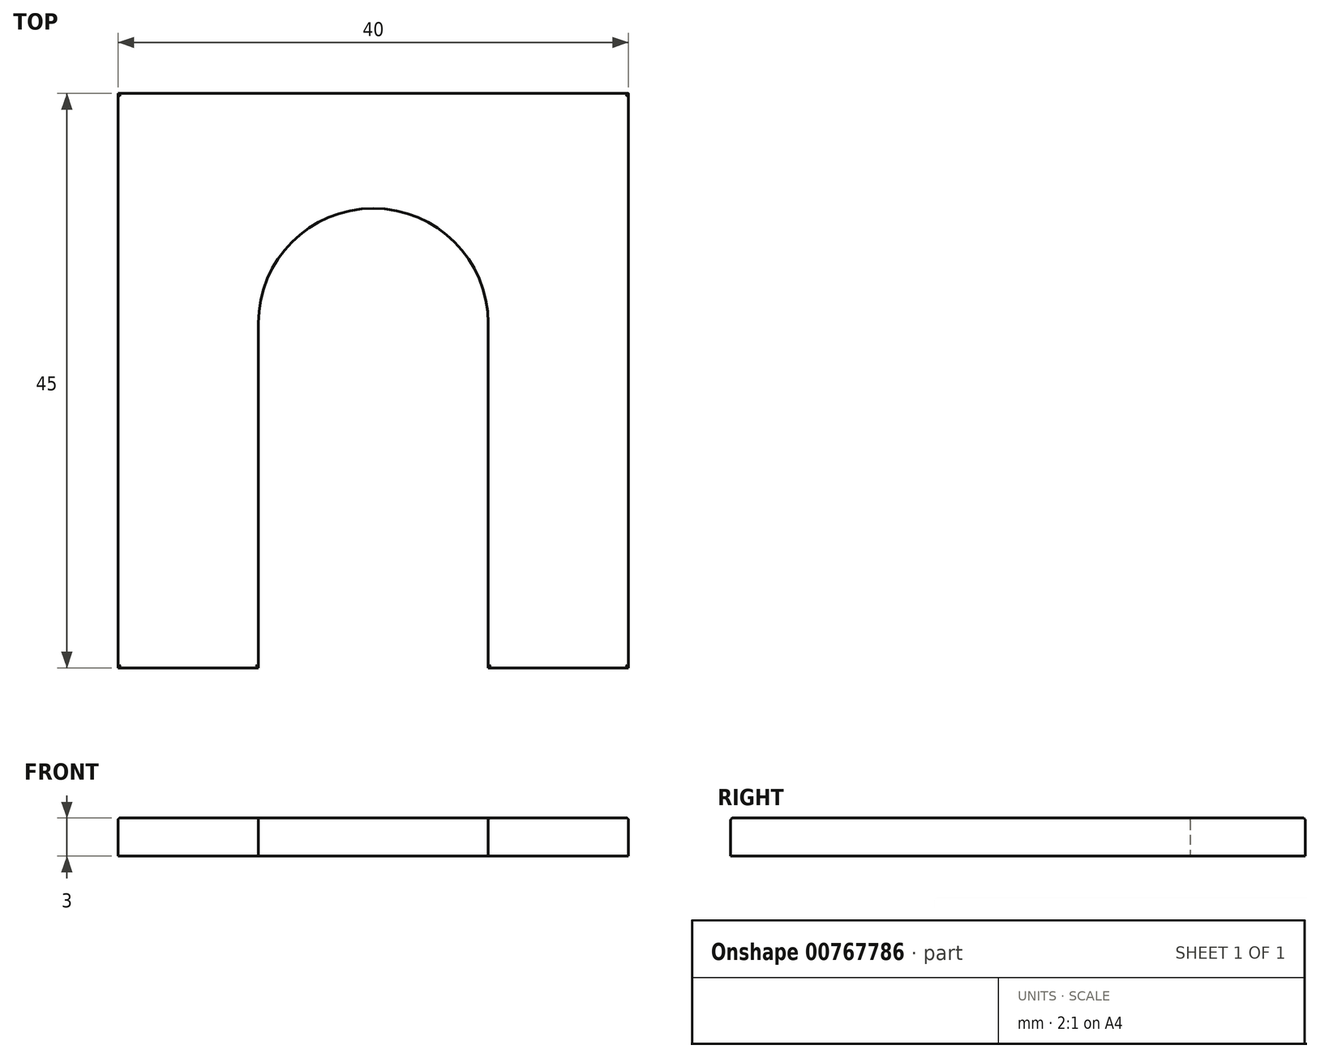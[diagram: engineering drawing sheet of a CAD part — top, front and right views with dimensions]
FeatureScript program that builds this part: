
annotation { "Feature Type Name" : "Feature", "Feature Type Description" : "" }
export const myFeature = defineFeature(function(context is Context, id is Id, definition is map)
    precondition{}
    {
        {
            var Q0;
            Q0=qCreatedBy(makeId("Top.planeOp"),FACE);
            var sketch = newSketch(context, id + "F0", { "sketchPlane" : qUnion([Q0])});
            skLineSegment(sketch, "E0", {"start": v(0, 0) * mm, "end": v(20, 0) * mm});
            skLineSegment(sketch, "E1", {"start": v(20, 0) * mm, "end": v(20, -45) * mm});
            skLineSegment(sketch, "E2", {"start": v(20, -45) * mm, "end": v(9, -45) * mm});
            skArc(sketch, "E3", {"start": v(9, -18) * mm, "mid": v(6.36, -11.64) * mm, "end": v(0, -9) * mm});
            skLineSegment(sketch, "E4", {"start": v(9, -45) * mm, "end": v(9, -18) * mm});
            skArc(sketch, "E5.MirrorCS", {"start": v(-9, -18) * mm, "mid": v(-6.36, -11.64) * mm, "end": v(0, -9) * mm});
            skLineSegment(sketch, "E6.MirrorCS", {"start": v(-9, -45) * mm, "end": v(-9, -18) * mm});
            skLineSegment(sketch, "E7.MirrorCS", {"start": v(-20, -45) * mm, "end": v(-9, -45) * mm});
            skLineSegment(sketch, "E8.MirrorCS", {"start": v(-20, 0) * mm, "end": v(-20, -45) * mm});
            skLineSegment(sketch, "E9.MirrorCS", {"start": v(0, 0) * mm, "end": v(-20, 0) * mm});
            skSolve(sketch);
        }
        {
            var Q0;
            Q0 = qSketchRegion(id + "F0", true);
            extrude(context, id + "F1", {"entities" : qUnion([Q0]), "depth" : 3 * mm, "offsetDistance" : 25 * mm});
        }
        {
            var Q0;
            Q0=makeQuery(id+"F1.opExtrude","CAP_FACE",FACE,{"disambiguationData":[OSD([sQuery(id+"F0.wireOp",EDGE,"E0"),sQuery(id+"F0.wireOp",EDGE,"E1"),sQuery(id+"F0.wireOp",EDGE,"E2"),sQuery(id+"F0.wireOp",EDGE,"E3"),sQuery(id+"F0.wireOp",EDGE,"E4"),sQuery(id+"F0.wireOp",EDGE,"E5.MirrorCS"),sQuery(id+"F0.wireOp",EDGE,"E6.MirrorCS"),sQuery(id+"F0.wireOp",EDGE,"E7.MirrorCS"),sQuery(id+"F0.wireOp",EDGE,"E8.MirrorCS"),sQuery(id+"F0.wireOp",EDGE,"E9.MirrorCS")])],"isStart":false});
            fillet(context, id + "F2", {"entities" : qUnion([Q0]), "radius" : 0.2 * mm, "tangentPropagation" : true, "allowEdgeOverflow" : false});
        }
    });
